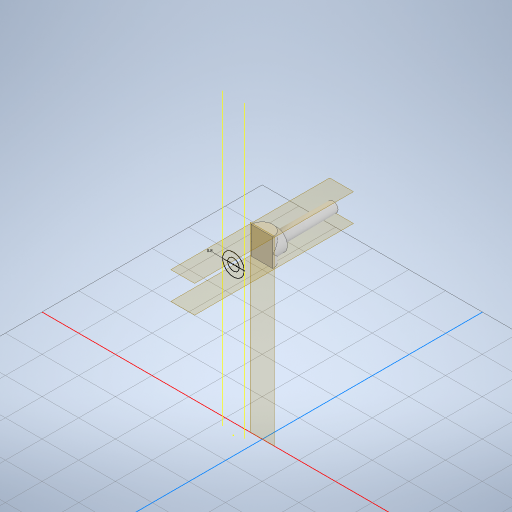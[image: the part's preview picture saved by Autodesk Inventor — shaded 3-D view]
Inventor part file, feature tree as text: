
AUTODESK INVENTOR PART (.ipt)
format: ipt  version: 2023 (Build 270158000, 158)  size: 358,400 bytes
history: native  units: in
note: dims shown in document units (in); Inventor stores cm internally (conversion verified against a paired STEP export)
features: extrude x10, sketch x7, plane x6, fillet x4, split x3
ambient origin geometry x8: Origin, YZ Plane, XZ Plane, XY Plane, X Axis, Y Axis, Z Axis, Center Point
bodies: Solid1 (feature_tree)
feature tree (30):
  extrude  "Extrusion1"  Depth=8.0709in TaperAngle=0.0deg
  sketch  "Sketch2"  dims[d3=0.2953in d4=0.7874in d5=0.6693in d6=0.0in]
  plane  "Work Plane1"
  extrude  "Extrusion2"  Depth=0.2953in TaperAngle=0.0deg
  sketch  "Sketch3"  dims[d7=0.1378in d8=0.2185in]
  extrude  "Extrusion3"  Depth=0.2185in
  extrude  "Extrusion4"  Depth=0.2185in
  plane  "Work Plane2"
  extrude  "Extrusion5"  Depth=1.5748in TaperAngle=0.0deg
  extrude  "Extrusion6"  Depth=0.5512in TaperAngle=0.0deg
  fillet  "Fillet1"  Radius=0.3051in
  fillet  "Fillet2"  Radius=0.3543in
  sketch  "Sketch5"  dims[d11=1.5748in d12=0.0in d13=0.5512in d14=0.0in]
  extrude  "Extrusion7"  Depth=0.0394in
  fillet  "Fillet3"  Radius=0.7874in
  sketch  "Sketch6"  dims[d15=-0.1969in d16=0.5512in d17=0.0in d18=0.3051in d19=0.3543in d20=0.0in]
  extrude  "Extrusion8"  Depth=0.75in TaperAngle=360.0deg
  extrude  "Extrusion10"  Depth=0.75in
  plane  "Work Plane3"
  plane  "Work Plane4"
  extrude  "Extrusion11"  Depth=0.75in TaperAngle=0.0deg
  fillet  "Fillet5"  Radius=0.0787in
  plane  "Work Plane6"
  split  "Split4"
  split  "Split5"
  split  "Split6"
  sketch  "Sketch1"  dims[d0=0.5906in d1=8.0709in d2=0.0in]
  sketch  "Sketch4"  dims[d9=0.2165in d10=0.2185in]
  sketch  "Sketch7"  dims[d21=0.0787in d22=0.0394in d23=0.7874in d25=0.0275in d27=1.1811in d29=360.0deg d31=0.1181in d32=0.3543in d33=0.0in d34=0.0787in d35=0.315in d36=0.7874in d37=0.0in d41=-0.3937in d42=0.3543in d43=-0.0103in d44=0.0in d45=3.937in d46=-0.0034in d47=0.0394in d48=3.6875in d49=0.75in]
  plane  "Work Plane5"
